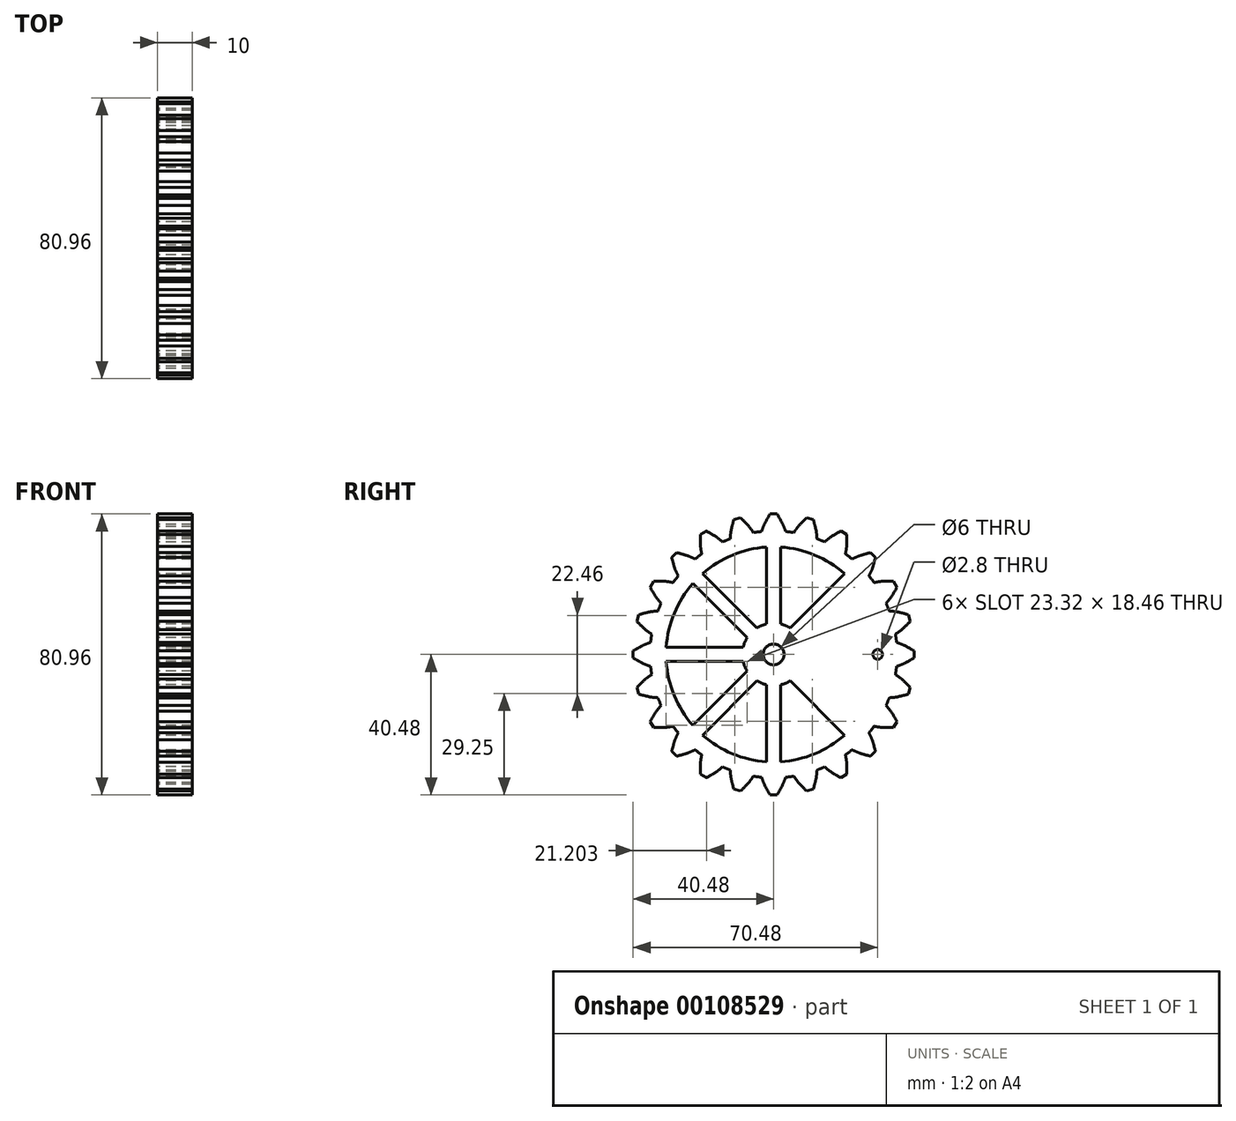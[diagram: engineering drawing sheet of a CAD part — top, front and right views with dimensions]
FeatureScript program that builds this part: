
annotation { "Feature Type Name" : "Feature", "Feature Type Description" : "" }
export const myFeature = defineFeature(function(context is Context, id is Id, definition is map)
    precondition{}
    {
        {
            var Q0;
            Q0=qCreatedBy(makeId("Right.planeOp"),FACE);
            var sketch = newSketch(context, id + "F0", { "sketchPlane" : qUnion([Q0])});
            skCircle(sketch, "E0", {"center": v(0, 0) * mm, "radius": 3 * mm});
            skArc(sketch, "E1", {"start": v(-2, 8.77) * mm, "mid": v(-3.44, 8.31) * mm, "end": v(-4.8, 7.62) * mm});
            skArc(sketch, "E2", {"start": v(-3.45, 35.43) * mm, "mid": v(-4.65, 35.3) * mm, "end": v(-5.84, 35.11) * mm});
            skArc(sketch, "E3", {"start": v(-2, 30.94) * mm, "mid": v(-11.86, 28.64) * mm, "end": v(-20.46, 23.29) * mm});
            skLineSegment(sketch, "E4.left", {"start": v(2, 8.77) * mm, "end": v(2, 30.94) * mm});
            skLineSegment(sketch, "E4.right", {"start": v(-2, 8.77) * mm, "end": v(-2, 30.94) * mm});
            skPoint(sketch, "E4.middle", {"position": v(0, 19.86) * mm});
            skArc(sketch, "E5", {"start": v(-2.7, 37.46) * mm, "mid": v(-3.1, 36.45) * mm, "end": v(-3.45, 35.43) * mm});
            skArc(sketch, "E6", {"start": v(-1, 40.48) * mm, "mid": v(-1.88, 38.99) * mm, "end": v(-2.7, 37.46) * mm});
            skLineSegment(sketch, "E7", {"start": v(-1, 40.48) * mm, "end": v(1, 40.48) * mm});
            skArc(sketch, "E8.MirrorCS", {"start": v(1, 40.48) * mm, "mid": v(1.88, 38.99) * mm, "end": v(2.7, 37.46) * mm});
            skArc(sketch, "E9.MirrorCS", {"start": v(2.7, 37.46) * mm, "mid": v(3.1, 36.45) * mm, "end": v(3.45, 35.43) * mm});
            skLineSegment(sketch, "E10.1.0", {"start": v(-4.8, 7.62) * mm, "end": v(-20.46, 23.29) * mm});
            skLineSegment(sketch, "E10.1.1", {"start": v(-7.62, 4.8) * mm, "end": v(-23.29, 20.46) * mm});
            skLineSegment(sketch, "E10.2.0", {"start": v(-8.77, 2) * mm, "end": v(-30.94, 2) * mm});
            skLineSegment(sketch, "E10.2.1", {"start": v(-8.77, -2) * mm, "end": v(-30.94, -2) * mm});
            skLineSegment(sketch, "E10.3.0", {"start": v(-7.62, -4.8) * mm, "end": v(-23.29, -20.46) * mm});
            skLineSegment(sketch, "E10.3.1", {"start": v(-4.8, -7.62) * mm, "end": v(-20.46, -23.29) * mm});
            skLineSegment(sketch, "E10.4.0", {"start": v(-2, -8.77) * mm, "end": v(-2, -30.94) * mm});
            skLineSegment(sketch, "E10.4.1", {"start": v(2, -8.77) * mm, "end": v(2, -30.94) * mm});
            skLineSegment(sketch, "E10.5.0", {"start": v(4.8, -7.62) * mm, "end": v(20.46, -23.29) * mm});
            skLineSegment(sketch, "E10.7.1", {"start": v(4.8, 7.62) * mm, "end": v(20.46, 23.29) * mm});
            skArc(sketch, "E11.trimOffspring", {"start": v(20.46, 23.29) * mm, "mid": v(11.86, 28.64) * mm, "end": v(2, 30.94) * mm});
            skArc(sketch, "E12.trimOffspring", {"start": v(4.8, 7.62) * mm, "mid": v(3.44, 8.31) * mm, "end": v(2, 8.77) * mm});
            skArc(sketch, "E13.trimOffspring", {"start": v(2, -8.77) * mm, "mid": v(3.44, -8.31) * mm, "end": v(4.8, -7.62) * mm});
            skArc(sketch, "E14.trimOffspring", {"start": v(2, -30.94) * mm, "mid": v(11.86, -28.64) * mm, "end": v(20.46, -23.29) * mm});
            skArc(sketch, "E15.trimOffspring", {"start": v(-20.46, -23.29) * mm, "mid": v(-11.86, -28.64) * mm, "end": v(-2, -30.94) * mm});
            skArc(sketch, "E16.trimOffspring", {"start": v(-4.8, -7.62) * mm, "mid": v(-3.44, -8.31) * mm, "end": v(-2, -8.77) * mm});
            skArc(sketch, "E17.trimOffspring", {"start": v(-8.77, -2) * mm, "mid": v(-8.31, -3.44) * mm, "end": v(-7.62, -4.8) * mm});
            skArc(sketch, "E18.trimOffspring", {"start": v(-30.94, -2) * mm, "mid": v(-28.64, -11.86) * mm, "end": v(-23.29, -20.46) * mm});
            skArc(sketch, "E19.trimOffspring", {"start": v(-23.29, 20.46) * mm, "mid": v(-28.64, 11.86) * mm, "end": v(-30.94, 2) * mm});
            skArc(sketch, "E20.trimOffspring", {"start": v(-7.62, 4.8) * mm, "mid": v(-8.31, 3.44) * mm, "end": v(-8.77, 2) * mm});
            skLineSegment(sketch, "E21", {"start": v(0, 0) * mm, "end": v(30, 0) * mm, "construction": true});
            skCircle(sketch, "E22", {"center": v(30, 0) * mm, "radius": 1.4 * mm});
            skLineSegment(sketch, "E23", {"start": v(0, 0) * mm, "end": v(0, 40.48) * mm, "construction": true});
            skLineSegment(sketch, "E24.1.0", {"start": v(0, 0) * mm, "end": v(-10.48, 39.1) * mm, "construction": true});
            skArc(sketch, "E24.1.1", {"start": v(-9.5, 39.36) * mm, "mid": v(-8.28, 38.14) * mm, "end": v(-7.1, 36.88) * mm});
            skArc(sketch, "E24.1.2", {"start": v(-7.1, 36.88) * mm, "mid": v(-6.45, 36.01) * mm, "end": v(-5.84, 35.11) * mm});
            skArc(sketch, "E24.1.3", {"start": v(-11.45, 38.84) * mm, "mid": v(-11.9, 37.17) * mm, "end": v(-12.3, 35.49) * mm});
            skLineSegment(sketch, "E24.1.4", {"start": v(-11.45, 38.84) * mm, "end": v(-9.5, 39.36) * mm});
            skArc(sketch, "E24.1.5", {"start": v(-12.3, 35.49) * mm, "mid": v(-12.42, 34.4) * mm, "end": v(-12.5, 33.33) * mm});
            skLineSegment(sketch, "E24.2.0", {"start": v(0, 0) * mm, "end": v(-20.24, 35.06) * mm, "construction": true});
            skArc(sketch, "E24.2.1", {"start": v(-19.37, 35.56) * mm, "mid": v(-17.87, 34.7) * mm, "end": v(-16.4, 33.79) * mm});
            skArc(sketch, "E24.2.2", {"start": v(-16.4, 33.79) * mm, "mid": v(-15.55, 33.12) * mm, "end": v(-14.73, 32.4) * mm});
            skArc(sketch, "E24.2.3", {"start": v(-21.11, 34.56) * mm, "mid": v(-21.12, 32.82) * mm, "end": v(-21.07, 31.1) * mm});
            skLineSegment(sketch, "E24.2.4", {"start": v(-21.11, 34.56) * mm, "end": v(-19.37, 35.56) * mm});
            skArc(sketch, "E24.2.5", {"start": v(-21.07, 31.1) * mm, "mid": v(-20.9, 30.02) * mm, "end": v(-20.7, 28.96) * mm});
            skLineSegment(sketch, "E25.1.3.0", {"start": v(0, 0) * mm, "end": v(-28.63, 28.63) * mm, "construction": true});
            skArc(sketch, "E25.3.3.0", {"start": v(-27.91, 29.34) * mm, "mid": v(-26.24, 28.9) * mm, "end": v(-24.58, 28.4) * mm});
            skArc(sketch, "E25.7.3.0", {"start": v(-24.58, 28.4) * mm, "mid": v(-23.59, 27.96) * mm, "end": v(-22.61, 27.5) * mm});
            skArc(sketch, "E25.11.3.0", {"start": v(-29.34, 27.91) * mm, "mid": v(-28.9, 26.24) * mm, "end": v(-28.4, 24.58) * mm});
            skLineSegment(sketch, "E25.15.3.0", {"start": v(-29.34, 27.91) * mm, "end": v(-27.91, 29.34) * mm});
            skArc(sketch, "E25.18.3.0", {"start": v(-28.4, 24.58) * mm, "mid": v(-27.96, 23.59) * mm, "end": v(-27.5, 22.61) * mm});
            skLineSegment(sketch, "E25.1.4.0", {"start": v(0, 0) * mm, "end": v(-35.06, 20.24) * mm, "construction": true});
            skArc(sketch, "E25.3.4.0", {"start": v(-34.56, 21.11) * mm, "mid": v(-32.82, 21.12) * mm, "end": v(-31.1, 21.07) * mm});
            skArc(sketch, "E25.7.4.0", {"start": v(-31.1, 21.07) * mm, "mid": v(-30.02, 20.9) * mm, "end": v(-28.96, 20.7) * mm});
            skArc(sketch, "E25.11.4.0", {"start": v(-35.56, 19.37) * mm, "mid": v(-34.7, 17.87) * mm, "end": v(-33.79, 16.4) * mm});
            skLineSegment(sketch, "E25.15.4.0", {"start": v(-35.56, 19.37) * mm, "end": v(-34.56, 21.11) * mm});
            skArc(sketch, "E25.18.4.0", {"start": v(-33.79, 16.4) * mm, "mid": v(-33.12, 15.55) * mm, "end": v(-32.4, 14.73) * mm});
            skLineSegment(sketch, "E25.1.5.0", {"start": v(0, 0) * mm, "end": v(-39.1, 10.48) * mm, "construction": true});
            skArc(sketch, "E25.3.5.0", {"start": v(-38.84, 11.45) * mm, "mid": v(-37.17, 11.9) * mm, "end": v(-35.49, 12.3) * mm});
            skArc(sketch, "E25.7.5.0", {"start": v(-35.49, 12.3) * mm, "mid": v(-34.4, 12.42) * mm, "end": v(-33.33, 12.5) * mm});
            skArc(sketch, "E25.11.5.0", {"start": v(-39.36, 9.5) * mm, "mid": v(-38.14, 8.28) * mm, "end": v(-36.88, 7.1) * mm});
            skLineSegment(sketch, "E25.15.5.0", {"start": v(-39.36, 9.5) * mm, "end": v(-38.84, 11.45) * mm});
            skArc(sketch, "E25.18.5.0", {"start": v(-36.88, 7.1) * mm, "mid": v(-36.01, 6.45) * mm, "end": v(-35.11, 5.84) * mm});
            skLineSegment(sketch, "E25.1.6.0", {"start": v(0, 0) * mm, "end": v(-40.48, 0) * mm, "construction": true});
            skArc(sketch, "E25.3.6.0", {"start": v(-40.48, 1) * mm, "mid": v(-38.99, 1.88) * mm, "end": v(-37.46, 2.7) * mm});
            skArc(sketch, "E25.7.6.0", {"start": v(-37.46, 2.7) * mm, "mid": v(-36.45, 3.1) * mm, "end": v(-35.43, 3.45) * mm});
            skArc(sketch, "E25.11.6.0", {"start": v(-40.48, -1) * mm, "mid": v(-38.99, -1.88) * mm, "end": v(-37.46, -2.7) * mm});
            skLineSegment(sketch, "E25.15.6.0", {"start": v(-40.48, -1) * mm, "end": v(-40.48, 1) * mm});
            skArc(sketch, "E25.18.6.0", {"start": v(-37.46, -2.7) * mm, "mid": v(-36.45, -3.1) * mm, "end": v(-35.43, -3.45) * mm});
            skLineSegment(sketch, "E25.1.7.0", {"start": v(0, 0) * mm, "end": v(-39.1, -10.48) * mm, "construction": true});
            skArc(sketch, "E25.3.7.0", {"start": v(-39.36, -9.5) * mm, "mid": v(-38.14, -8.28) * mm, "end": v(-36.88, -7.1) * mm});
            skArc(sketch, "E25.7.7.0", {"start": v(-36.88, -7.1) * mm, "mid": v(-36.01, -6.45) * mm, "end": v(-35.11, -5.84) * mm});
            skArc(sketch, "E25.11.7.0", {"start": v(-38.84, -11.45) * mm, "mid": v(-37.17, -11.9) * mm, "end": v(-35.49, -12.3) * mm});
            skLineSegment(sketch, "E25.15.7.0", {"start": v(-38.84, -11.45) * mm, "end": v(-39.36, -9.5) * mm});
            skArc(sketch, "E25.18.7.0", {"start": v(-35.49, -12.3) * mm, "mid": v(-34.4, -12.42) * mm, "end": v(-33.33, -12.5) * mm});
            skLineSegment(sketch, "E25.1.8.0", {"start": v(0, 0) * mm, "end": v(-35.06, -20.24) * mm, "construction": true});
            skArc(sketch, "E25.3.8.0", {"start": v(-35.56, -19.37) * mm, "mid": v(-34.7, -17.87) * mm, "end": v(-33.79, -16.4) * mm});
            skArc(sketch, "E25.7.8.0", {"start": v(-33.79, -16.4) * mm, "mid": v(-33.12, -15.55) * mm, "end": v(-32.4, -14.73) * mm});
            skArc(sketch, "E25.11.8.0", {"start": v(-34.56, -21.11) * mm, "mid": v(-32.82, -21.12) * mm, "end": v(-31.1, -21.07) * mm});
            skLineSegment(sketch, "E25.15.8.0", {"start": v(-34.56, -21.11) * mm, "end": v(-35.56, -19.37) * mm});
            skArc(sketch, "E25.18.8.0", {"start": v(-31.1, -21.07) * mm, "mid": v(-30.02, -20.9) * mm, "end": v(-28.96, -20.7) * mm});
            skLineSegment(sketch, "E25.1.9.0", {"start": v(0, 0) * mm, "end": v(-28.63, -28.63) * mm, "construction": true});
            skArc(sketch, "E25.3.9.0", {"start": v(-29.34, -27.91) * mm, "mid": v(-28.9, -26.24) * mm, "end": v(-28.4, -24.58) * mm});
            skArc(sketch, "E25.7.9.0", {"start": v(-28.4, -24.58) * mm, "mid": v(-27.96, -23.59) * mm, "end": v(-27.5, -22.61) * mm});
            skArc(sketch, "E25.11.9.0", {"start": v(-27.91, -29.34) * mm, "mid": v(-26.24, -28.9) * mm, "end": v(-24.58, -28.4) * mm});
            skLineSegment(sketch, "E25.15.9.0", {"start": v(-27.91, -29.34) * mm, "end": v(-29.34, -27.91) * mm});
            skArc(sketch, "E25.18.9.0", {"start": v(-24.58, -28.4) * mm, "mid": v(-23.59, -27.96) * mm, "end": v(-22.61, -27.5) * mm});
            skLineSegment(sketch, "E25.1.10.0", {"start": v(0, 0) * mm, "end": v(-20.24, -35.06) * mm, "construction": true});
            skArc(sketch, "E25.3.10.0", {"start": v(-21.11, -34.56) * mm, "mid": v(-21.12, -32.82) * mm, "end": v(-21.07, -31.1) * mm});
            skArc(sketch, "E25.7.10.0", {"start": v(-21.07, -31.1) * mm, "mid": v(-20.9, -30.02) * mm, "end": v(-20.7, -28.96) * mm});
            skArc(sketch, "E25.11.10.0", {"start": v(-19.37, -35.56) * mm, "mid": v(-17.87, -34.7) * mm, "end": v(-16.4, -33.79) * mm});
            skLineSegment(sketch, "E25.15.10.0", {"start": v(-19.37, -35.56) * mm, "end": v(-21.11, -34.56) * mm});
            skArc(sketch, "E25.18.10.0", {"start": v(-16.4, -33.79) * mm, "mid": v(-15.55, -33.12) * mm, "end": v(-14.73, -32.4) * mm});
            skLineSegment(sketch, "E25.1.11.0", {"start": v(0, 0) * mm, "end": v(-10.48, -39.1) * mm, "construction": true});
            skArc(sketch, "E25.3.11.0", {"start": v(-11.45, -38.84) * mm, "mid": v(-11.9, -37.17) * mm, "end": v(-12.3, -35.49) * mm});
            skArc(sketch, "E25.7.11.0", {"start": v(-12.3, -35.49) * mm, "mid": v(-12.42, -34.4) * mm, "end": v(-12.5, -33.33) * mm});
            skArc(sketch, "E25.11.11.0", {"start": v(-9.5, -39.36) * mm, "mid": v(-8.28, -38.14) * mm, "end": v(-7.1, -36.88) * mm});
            skLineSegment(sketch, "E25.15.11.0", {"start": v(-9.5, -39.36) * mm, "end": v(-11.45, -38.84) * mm});
            skArc(sketch, "E25.18.11.0", {"start": v(-7.1, -36.88) * mm, "mid": v(-6.45, -36.01) * mm, "end": v(-5.84, -35.11) * mm});
            skLineSegment(sketch, "E25.1.12.0", {"start": v(0, 0) * mm, "end": v(0, -40.48) * mm, "construction": true});
            skArc(sketch, "E25.3.12.0", {"start": v(-1, -40.48) * mm, "mid": v(-1.88, -38.99) * mm, "end": v(-2.7, -37.46) * mm});
            skArc(sketch, "E25.7.12.0", {"start": v(-2.7, -37.46) * mm, "mid": v(-3.1, -36.45) * mm, "end": v(-3.45, -35.43) * mm});
            skArc(sketch, "E25.11.12.0", {"start": v(1, -40.48) * mm, "mid": v(1.88, -38.99) * mm, "end": v(2.7, -37.46) * mm});
            skLineSegment(sketch, "E25.15.12.0", {"start": v(1, -40.48) * mm, "end": v(-1, -40.48) * mm});
            skArc(sketch, "E25.18.12.0", {"start": v(2.7, -37.46) * mm, "mid": v(3.1, -36.45) * mm, "end": v(3.45, -35.43) * mm});
            skLineSegment(sketch, "E25.1.13.0", {"start": v(0, 0) * mm, "end": v(10.48, -39.1) * mm, "construction": true});
            skArc(sketch, "E25.3.13.0", {"start": v(9.5, -39.36) * mm, "mid": v(8.28, -38.14) * mm, "end": v(7.1, -36.88) * mm});
            skArc(sketch, "E25.7.13.0", {"start": v(7.1, -36.88) * mm, "mid": v(6.45, -36.01) * mm, "end": v(5.84, -35.11) * mm});
            skArc(sketch, "E25.11.13.0", {"start": v(11.45, -38.84) * mm, "mid": v(11.9, -37.17) * mm, "end": v(12.3, -35.49) * mm});
            skLineSegment(sketch, "E25.15.13.0", {"start": v(11.45, -38.84) * mm, "end": v(9.5, -39.36) * mm});
            skArc(sketch, "E25.18.13.0", {"start": v(12.3, -35.49) * mm, "mid": v(12.42, -34.4) * mm, "end": v(12.5, -33.33) * mm});
            skLineSegment(sketch, "E25.1.14.0", {"start": v(0, 0) * mm, "end": v(20.24, -35.06) * mm, "construction": true});
            skArc(sketch, "E25.3.14.0", {"start": v(19.37, -35.56) * mm, "mid": v(17.87, -34.7) * mm, "end": v(16.4, -33.79) * mm});
            skArc(sketch, "E25.7.14.0", {"start": v(16.4, -33.79) * mm, "mid": v(15.55, -33.12) * mm, "end": v(14.73, -32.4) * mm});
            skArc(sketch, "E25.11.14.0", {"start": v(21.11, -34.56) * mm, "mid": v(21.12, -32.82) * mm, "end": v(21.07, -31.1) * mm});
            skLineSegment(sketch, "E25.15.14.0", {"start": v(21.11, -34.56) * mm, "end": v(19.37, -35.56) * mm});
            skArc(sketch, "E25.18.14.0", {"start": v(21.07, -31.1) * mm, "mid": v(20.9, -30.02) * mm, "end": v(20.7, -28.96) * mm});
            skLineSegment(sketch, "E25.1.15.0", {"start": v(0, 0) * mm, "end": v(28.63, -28.63) * mm, "construction": true});
            skArc(sketch, "E25.3.15.0", {"start": v(27.91, -29.34) * mm, "mid": v(26.24, -28.9) * mm, "end": v(24.58, -28.4) * mm});
            skArc(sketch, "E25.7.15.0", {"start": v(24.58, -28.4) * mm, "mid": v(23.59, -27.96) * mm, "end": v(22.61, -27.5) * mm});
            skArc(sketch, "E25.11.15.0", {"start": v(29.34, -27.91) * mm, "mid": v(28.9, -26.24) * mm, "end": v(28.4, -24.58) * mm});
            skLineSegment(sketch, "E25.15.15.0", {"start": v(29.34, -27.91) * mm, "end": v(27.91, -29.34) * mm});
            skArc(sketch, "E25.18.15.0", {"start": v(28.4, -24.58) * mm, "mid": v(27.96, -23.59) * mm, "end": v(27.5, -22.61) * mm});
            skLineSegment(sketch, "E25.1.16.0", {"start": v(0, 0) * mm, "end": v(35.06, -20.24) * mm, "construction": true});
            skArc(sketch, "E25.3.16.0", {"start": v(34.56, -21.11) * mm, "mid": v(32.82, -21.12) * mm, "end": v(31.1, -21.07) * mm});
            skArc(sketch, "E25.7.16.0", {"start": v(31.1, -21.07) * mm, "mid": v(30.02, -20.9) * mm, "end": v(28.96, -20.7) * mm});
            skArc(sketch, "E25.11.16.0", {"start": v(35.56, -19.37) * mm, "mid": v(34.7, -17.87) * mm, "end": v(33.79, -16.4) * mm});
            skLineSegment(sketch, "E25.15.16.0", {"start": v(35.56, -19.37) * mm, "end": v(34.56, -21.11) * mm});
            skArc(sketch, "E25.18.16.0", {"start": v(33.79, -16.4) * mm, "mid": v(33.12, -15.55) * mm, "end": v(32.4, -14.73) * mm});
            skLineSegment(sketch, "E25.1.17.0", {"start": v(0, 0) * mm, "end": v(39.1, -10.48) * mm, "construction": true});
            skArc(sketch, "E25.3.17.0", {"start": v(38.84, -11.45) * mm, "mid": v(37.17, -11.9) * mm, "end": v(35.49, -12.3) * mm});
            skArc(sketch, "E25.7.17.0", {"start": v(35.49, -12.3) * mm, "mid": v(34.4, -12.42) * mm, "end": v(33.33, -12.5) * mm});
            skArc(sketch, "E25.11.17.0", {"start": v(39.36, -9.5) * mm, "mid": v(38.14, -8.28) * mm, "end": v(36.88, -7.1) * mm});
            skLineSegment(sketch, "E25.15.17.0", {"start": v(39.36, -9.5) * mm, "end": v(38.84, -11.45) * mm});
            skArc(sketch, "E25.18.17.0", {"start": v(36.88, -7.1) * mm, "mid": v(36.01, -6.45) * mm, "end": v(35.11, -5.84) * mm});
            skLineSegment(sketch, "E25.1.18.0", {"start": v(0, 0) * mm, "end": v(40.48, 0) * mm, "construction": true});
            skArc(sketch, "E25.3.18.0", {"start": v(40.48, -1) * mm, "mid": v(38.99, -1.88) * mm, "end": v(37.46, -2.7) * mm});
            skArc(sketch, "E25.7.18.0", {"start": v(37.46, -2.7) * mm, "mid": v(36.45, -3.1) * mm, "end": v(35.43, -3.45) * mm});
            skArc(sketch, "E25.11.18.0", {"start": v(40.48, 1) * mm, "mid": v(38.99, 1.88) * mm, "end": v(37.46, 2.7) * mm});
            skLineSegment(sketch, "E25.15.18.0", {"start": v(40.48, 1) * mm, "end": v(40.48, -1) * mm});
            skArc(sketch, "E25.18.18.0", {"start": v(37.46, 2.7) * mm, "mid": v(36.45, 3.1) * mm, "end": v(35.43, 3.45) * mm});
            skLineSegment(sketch, "E25.1.19.0", {"start": v(0, 0) * mm, "end": v(39.1, 10.48) * mm, "construction": true});
            skArc(sketch, "E25.3.19.0", {"start": v(39.36, 9.5) * mm, "mid": v(38.14, 8.28) * mm, "end": v(36.88, 7.1) * mm});
            skArc(sketch, "E25.7.19.0", {"start": v(36.88, 7.1) * mm, "mid": v(36.01, 6.45) * mm, "end": v(35.11, 5.84) * mm});
            skArc(sketch, "E25.11.19.0", {"start": v(38.84, 11.45) * mm, "mid": v(37.17, 11.9) * mm, "end": v(35.49, 12.3) * mm});
            skLineSegment(sketch, "E25.15.19.0", {"start": v(38.84, 11.45) * mm, "end": v(39.36, 9.5) * mm});
            skArc(sketch, "E25.18.19.0", {"start": v(35.49, 12.3) * mm, "mid": v(34.4, 12.42) * mm, "end": v(33.33, 12.5) * mm});
            skLineSegment(sketch, "E25.1.20.0", {"start": v(0, 0) * mm, "end": v(35.06, 20.24) * mm, "construction": true});
            skArc(sketch, "E25.3.20.0", {"start": v(35.56, 19.37) * mm, "mid": v(34.7, 17.87) * mm, "end": v(33.79, 16.4) * mm});
            skArc(sketch, "E25.7.20.0", {"start": v(33.79, 16.4) * mm, "mid": v(33.12, 15.55) * mm, "end": v(32.4, 14.73) * mm});
            skArc(sketch, "E25.11.20.0", {"start": v(34.56, 21.11) * mm, "mid": v(32.82, 21.12) * mm, "end": v(31.1, 21.07) * mm});
            skLineSegment(sketch, "E25.15.20.0", {"start": v(34.56, 21.11) * mm, "end": v(35.56, 19.37) * mm});
            skArc(sketch, "E25.18.20.0", {"start": v(31.1, 21.07) * mm, "mid": v(30.02, 20.9) * mm, "end": v(28.96, 20.7) * mm});
            skLineSegment(sketch, "E25.1.21.0", {"start": v(0, 0) * mm, "end": v(28.63, 28.63) * mm, "construction": true});
            skArc(sketch, "E25.3.21.0", {"start": v(29.34, 27.91) * mm, "mid": v(28.9, 26.24) * mm, "end": v(28.4, 24.58) * mm});
            skArc(sketch, "E25.7.21.0", {"start": v(28.4, 24.58) * mm, "mid": v(27.96, 23.59) * mm, "end": v(27.5, 22.61) * mm});
            skArc(sketch, "E25.11.21.0", {"start": v(27.91, 29.34) * mm, "mid": v(26.24, 28.9) * mm, "end": v(24.58, 28.4) * mm});
            skLineSegment(sketch, "E25.15.21.0", {"start": v(27.91, 29.34) * mm, "end": v(29.34, 27.91) * mm});
            skArc(sketch, "E25.18.21.0", {"start": v(24.58, 28.4) * mm, "mid": v(23.59, 27.96) * mm, "end": v(22.61, 27.5) * mm});
            skLineSegment(sketch, "E25.1.22.0", {"start": v(0, 0) * mm, "end": v(20.24, 35.06) * mm, "construction": true});
            skArc(sketch, "E25.3.22.0", {"start": v(21.11, 34.56) * mm, "mid": v(21.12, 32.82) * mm, "end": v(21.07, 31.1) * mm});
            skArc(sketch, "E25.7.22.0", {"start": v(21.07, 31.1) * mm, "mid": v(20.9, 30.02) * mm, "end": v(20.7, 28.96) * mm});
            skArc(sketch, "E25.11.22.0", {"start": v(19.37, 35.56) * mm, "mid": v(17.87, 34.7) * mm, "end": v(16.4, 33.79) * mm});
            skLineSegment(sketch, "E25.15.22.0", {"start": v(19.37, 35.56) * mm, "end": v(21.11, 34.56) * mm});
            skArc(sketch, "E25.18.22.0", {"start": v(16.4, 33.79) * mm, "mid": v(15.55, 33.12) * mm, "end": v(14.73, 32.4) * mm});
            skLineSegment(sketch, "E25.1.23.0", {"start": v(0, 0) * mm, "end": v(10.48, 39.1) * mm, "construction": true});
            skArc(sketch, "E25.3.23.0", {"start": v(11.45, 38.84) * mm, "mid": v(11.9, 37.17) * mm, "end": v(12.3, 35.49) * mm});
            skArc(sketch, "E25.7.23.0", {"start": v(12.3, 35.49) * mm, "mid": v(12.42, 34.4) * mm, "end": v(12.5, 33.33) * mm});
            skArc(sketch, "E25.11.23.0", {"start": v(9.5, 39.36) * mm, "mid": v(8.28, 38.14) * mm, "end": v(7.1, 36.88) * mm});
            skLineSegment(sketch, "E25.15.23.0", {"start": v(9.5, 39.36) * mm, "end": v(11.45, 38.84) * mm});
            skArc(sketch, "E25.18.23.0", {"start": v(7.1, 36.88) * mm, "mid": v(6.45, 36.01) * mm, "end": v(5.84, 35.11) * mm});
            skArc(sketch, "E26.trimOffspring", {"start": v(5.84, 35.11) * mm, "mid": v(4.65, 35.3) * mm, "end": v(3.45, 35.43) * mm});
            skArc(sketch, "E27.trimOffspring", {"start": v(14.73, 32.4) * mm, "mid": v(13.62, 32.89) * mm, "end": v(12.5, 33.33) * mm});
            skArc(sketch, "E28.trimOffspring", {"start": v(22.61, 27.5) * mm, "mid": v(21.67, 28.24) * mm, "end": v(20.7, 28.96) * mm});
            skArc(sketch, "E29.trimOffspring", {"start": v(28.96, 20.7) * mm, "mid": v(28.24, 21.67) * mm, "end": v(27.5, 22.61) * mm});
            skArc(sketch, "E30.trimOffspring", {"start": v(33.33, 12.5) * mm, "mid": v(32.89, 13.62) * mm, "end": v(32.4, 14.73) * mm});
            skArc(sketch, "E31.trimOffspring", {"start": v(35.43, 3.45) * mm, "mid": v(35.3, 4.65) * mm, "end": v(35.11, 5.84) * mm});
            skArc(sketch, "E32.trimOffspring", {"start": v(-12.5, 33.33) * mm, "mid": v(-13.62, 32.89) * mm, "end": v(-14.73, 32.4) * mm});
            skArc(sketch, "E33.trimOffspring", {"start": v(-27.5, 22.61) * mm, "mid": v(-28.24, 21.67) * mm, "end": v(-28.96, 20.7) * mm});
            skArc(sketch, "E34.trimOffspring", {"start": v(-32.4, 14.73) * mm, "mid": v(-32.89, 13.62) * mm, "end": v(-33.33, 12.5) * mm});
            skArc(sketch, "E35.trimOffspring", {"start": v(-35.11, 5.84) * mm, "mid": v(-35.3, 4.65) * mm, "end": v(-35.43, 3.45) * mm});
            skArc(sketch, "E36.trimOffspring", {"start": v(-35.43, -3.45) * mm, "mid": v(-35.3, -4.65) * mm, "end": v(-35.11, -5.84) * mm});
            skArc(sketch, "E37.trimOffspring", {"start": v(-33.33, -12.5) * mm, "mid": v(-32.89, -13.62) * mm, "end": v(-32.4, -14.73) * mm});
            skArc(sketch, "E38.trimOffspring", {"start": v(-28.96, -20.7) * mm, "mid": v(-28.24, -21.67) * mm, "end": v(-27.5, -22.61) * mm});
            skArc(sketch, "E39.trimOffspring", {"start": v(-22.61, -27.5) * mm, "mid": v(-21.67, -28.24) * mm, "end": v(-20.7, -28.96) * mm});
            skArc(sketch, "E40.trimOffspring", {"start": v(-14.73, -32.4) * mm, "mid": v(-13.62, -32.89) * mm, "end": v(-12.5, -33.33) * mm});
            skArc(sketch, "E41.trimOffspring", {"start": v(-5.84, -35.11) * mm, "mid": v(-4.65, -35.3) * mm, "end": v(-3.45, -35.43) * mm});
            skArc(sketch, "E42.trimOffspring", {"start": v(3.45, -35.43) * mm, "mid": v(4.65, -35.3) * mm, "end": v(5.84, -35.11) * mm});
            skArc(sketch, "E43.trimOffspring", {"start": v(35.11, -5.84) * mm, "mid": v(35.3, -4.65) * mm, "end": v(35.43, -3.45) * mm});
            skArc(sketch, "E44.trimOffspring", {"start": v(32.4, -14.73) * mm, "mid": v(32.89, -13.62) * mm, "end": v(33.33, -12.5) * mm});
            skArc(sketch, "E45.trimOffspring", {"start": v(27.5, -22.61) * mm, "mid": v(28.24, -21.67) * mm, "end": v(28.96, -20.7) * mm});
            skArc(sketch, "E46.trimOffspring", {"start": v(20.7, -28.96) * mm, "mid": v(21.67, -28.24) * mm, "end": v(22.61, -27.5) * mm});
            skArc(sketch, "E47.trimOffspring", {"start": v(12.5, -33.33) * mm, "mid": v(13.62, -32.89) * mm, "end": v(14.73, -32.4) * mm});
            skArc(sketch, "E48", {"start": v(-22.61, 27.5) * mm, "mid": v(-21.67, 28.24) * mm, "end": v(-20.7, 28.96) * mm});
            skSolve(sketch);
        }
        {
            var Q0;
            Q0=makeQuery(id+"F0.imprint","IMPRINT",FACE,{"disambiguationData":[TD([[makeQuery(id+"F0.imprint","IMPRINT",EDGE,{"derivedFrom":sQuery(id+"F0.wireOp",EDGE,"E0")}),-1.0]])]});
            extrude(context, id + "F1", {"entities" : qUnion([Q0]), "depth" : 10 * mm});
        }
    });
